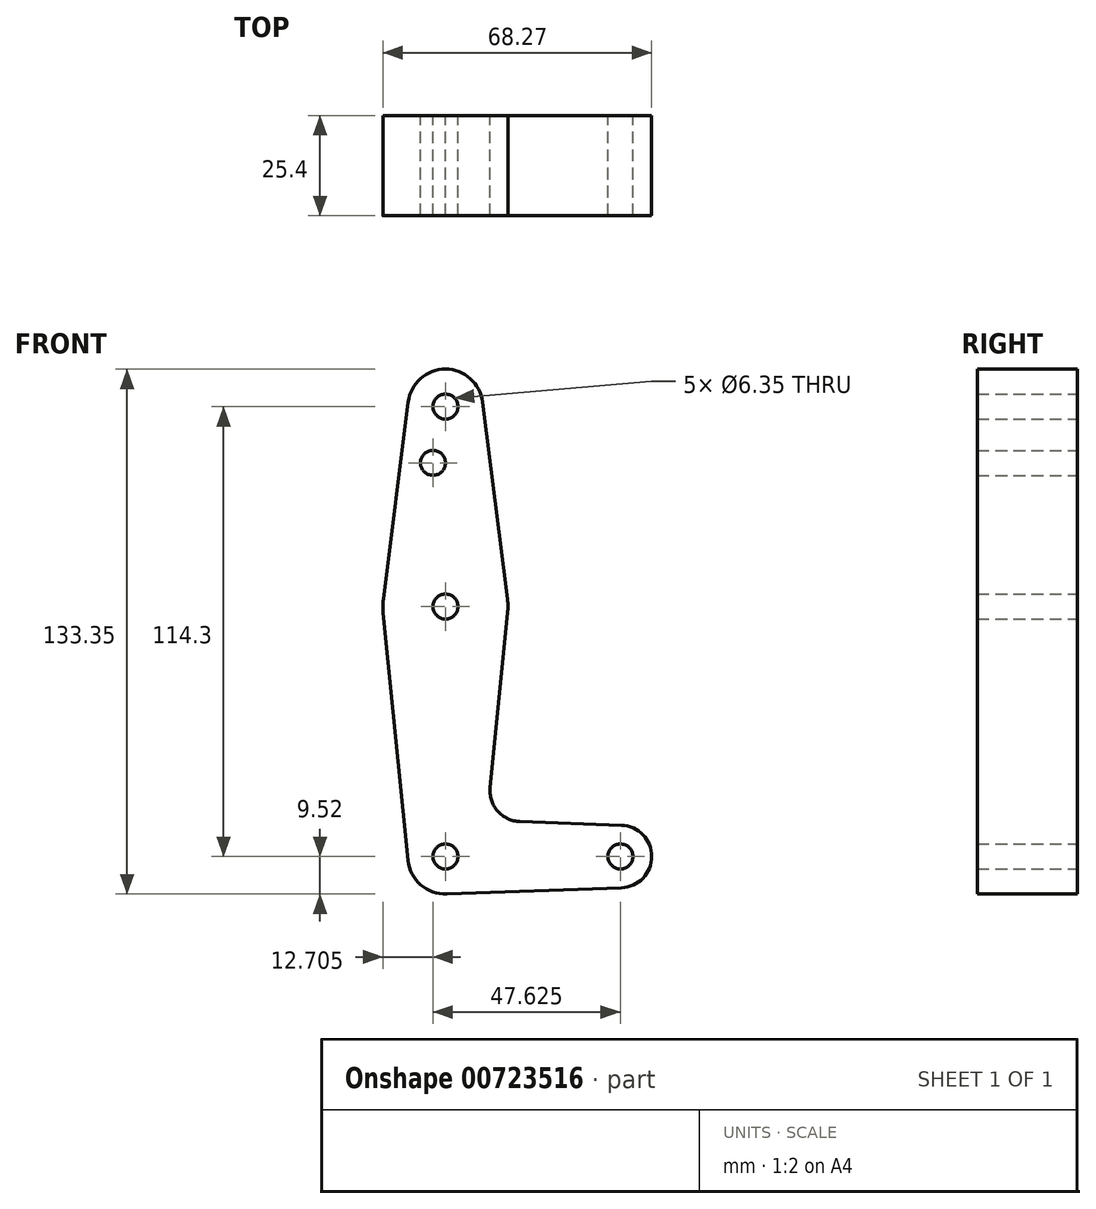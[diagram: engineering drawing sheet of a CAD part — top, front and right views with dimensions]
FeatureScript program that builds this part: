
annotation { "Feature Type Name" : "Feature", "Feature Type Description" : "" }
export const myFeature = defineFeature(function(context is Context, id is Id, definition is map)
    precondition{}
    {
        {
            var Q0;
            Q0=qCreatedBy(makeId("Front.planeOp"),FACE);
            var sketch = newSketch(context, id + "F0", { "sketchPlane" : qUnion([Q0])});
            skLineSegment(sketch, "E0", {"start": v(0, 114.3) * mm, "end": v(0, 0) * mm, "construction": true});
            skLineSegment(sketch, "E1", {"start": v(0, 0) * mm, "end": v(44.45, 0) * mm, "construction": true});
            skCircle(sketch, "E2", {"center": v(0, 114.3) * mm, "radius": 9.53 * mm});
            skCircle(sketch, "E3", {"center": v(0, 63.5) * mm, "radius": 15.88 * mm});
            skCircle(sketch, "E4", {"center": v(0, 0) * mm, "radius": 9.53 * mm});
            skCircle(sketch, "E5", {"center": v(44.45, 0) * mm, "radius": 7.94 * mm});
            skLineSegment(sketch, "E6", {"start": v(9.45, 115.5) * mm, "end": v(15.75, 65.48) * mm});
            skLineSegment(sketch, "E7", {"start": v(-9.45, 115.5) * mm, "end": v(-15.75, 65.48) * mm});
            skLineSegment(sketch, "E8", {"start": v(15.97, 63.64) * mm, "end": v(11.34, 17.6) * mm});
            skLineSegment(sketch, "E9", {"start": v(-15.8, 61.91) * mm, "end": v(-9.48, -0.95) * mm});
            skLineSegment(sketch, "E10", {"start": v(18.97, 8.85) * mm, "end": v(44.73, 7.93) * mm});
            skLineSegment(sketch, "E11", {"start": v(0.34, -9.52) * mm, "end": v(44.73, -7.93) * mm});
            skCircle(sketch, "E12", {"center": v(0, 114.3) * mm, "radius": 3.18 * mm});
            skCircle(sketch, "E13", {"center": v(-3.17, 100.03) * mm, "radius": 3.18 * mm});
            skCircle(sketch, "E14", {"center": v(0, 63.5) * mm, "radius": 3.18 * mm});
            skCircle(sketch, "E15", {"center": v(0, 0) * mm, "radius": 3.18 * mm});
            skCircle(sketch, "E16", {"center": v(44.45, 0) * mm, "radius": 3.18 * mm});
            skArc(sketch, "E17.filletArc", {"start": v(11.34, 17.6) * mm, "mid": v(13.26, 11.57) * mm, "end": v(18.97, 8.85) * mm});
            skSolve(sketch);
        }
        {
            var Q0;
            Q0 = qSketchRegion(id + "F0", true);
            extrude(context, id + "F1", {"entities" : qUnion([Q0]), "depth" : 25.4 * mm, "offsetDistance" : 25.4 * mm});
        }
    });
